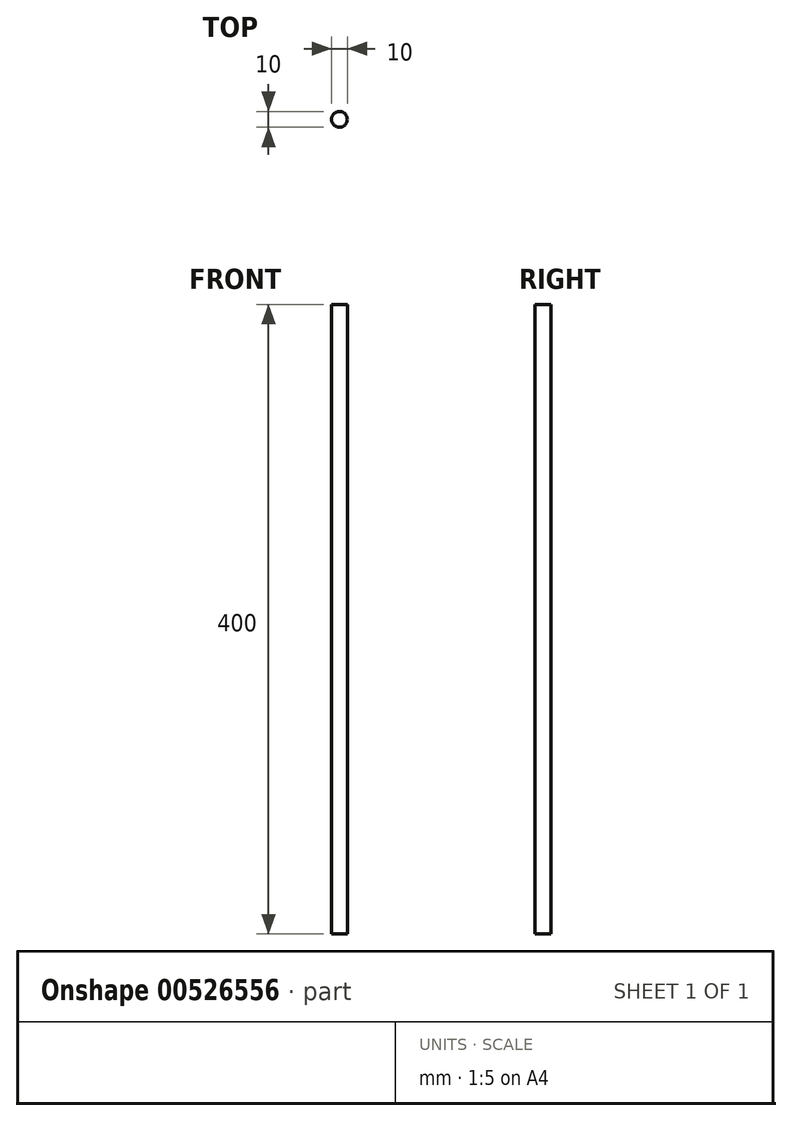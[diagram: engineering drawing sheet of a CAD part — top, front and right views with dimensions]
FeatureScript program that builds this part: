
annotation { "Feature Type Name" : "Feature", "Feature Type Description" : "" }
export const myFeature = defineFeature(function(context is Context, id is Id, definition is map)
    precondition{}
    {
        {
            var Q0;
            Q0=qCreatedBy(makeId("Top.planeOp"),FACE);
            var sketch = newSketch(context, id + "F0", { "sketchPlane" : qUnion([Q0])});
            skCircle(sketch, "E0", {"center": v(0, 0) * mm, "radius": 5 * mm});
            skSolve(sketch);
        }
        {
            var Q0;
            Q0=qSketchRegion(id+"F0",true);
            extrude(context, id + "F1", {"entities" : qUnion([Q0]), "depth" : 400 * mm, "offsetDistance" : 25 * mm});
        }
    });
